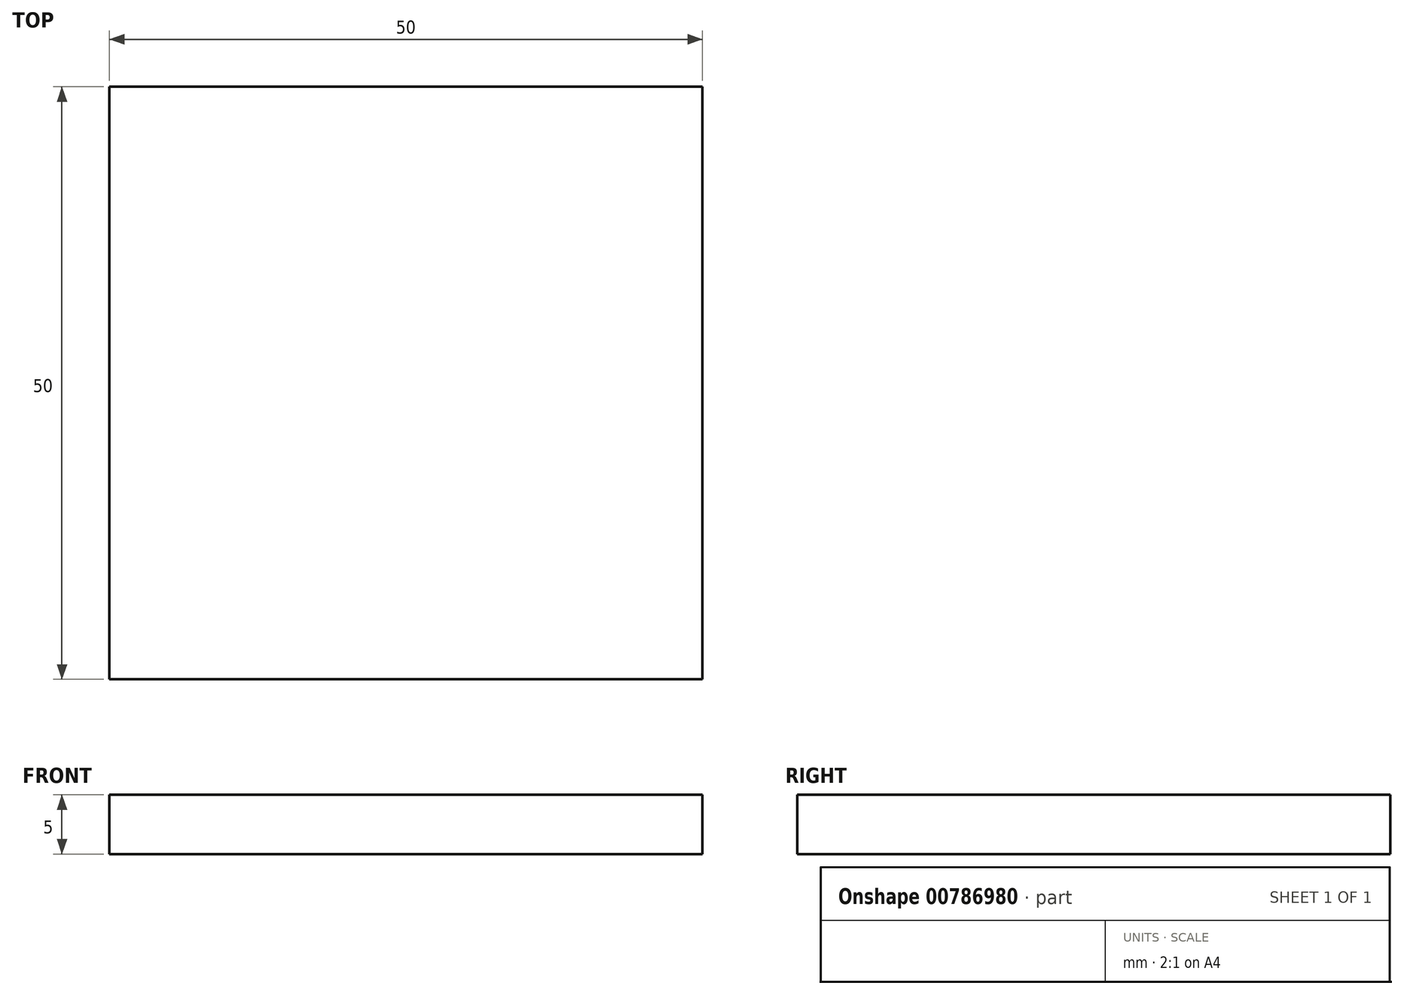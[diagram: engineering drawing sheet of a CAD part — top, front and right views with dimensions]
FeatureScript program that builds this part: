
annotation { "Feature Type Name" : "Feature", "Feature Type Description" : "" }
export const myFeature = defineFeature(function(context is Context, id is Id, definition is map)
    precondition{}
    {
        {
            var Q0;
            Q0=qCreatedBy(makeId("Top.planeOp"),FACE);
            var sketch = newSketch(context, id + "F0", { "sketchPlane" : qUnion([Q0])});
            skLineSegment(sketch, "E0.bottom", {"start": v(25, -25) * mm, "end": v(-25, -25) * mm});
            skLineSegment(sketch, "E0.top", {"start": v(25, 25) * mm, "end": v(-25, 25) * mm});
            skLineSegment(sketch, "E0.left", {"start": v(25, -25) * mm, "end": v(25, 25) * mm});
            skLineSegment(sketch, "E0.right", {"start": v(-25, -25) * mm, "end": v(-25, 25) * mm});
            skPoint(sketch, "E0.middle", {"position": v(0, 0) * mm});
            skSolve(sketch);
        }
        {
            var Q0;
            Q0 = qSketchRegion(id + "F0", true);
            extrude(context, id + "F1", {"entities" : qUnion([Q0]), "depth" : 5 * mm, "offsetDistance" : 25 * mm});
        }
    });
